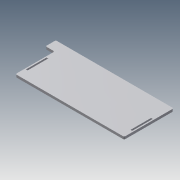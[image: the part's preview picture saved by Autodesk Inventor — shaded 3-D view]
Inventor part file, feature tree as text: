
AUTODESK INVENTOR PART (.ipt)
format: ipt  version: 2014 (Build 180170000, 170)  size: 117,248 bytes
history: native  units: mm
features: extrude x3, sketch x3, fillet x2
ambient origin geometry x8: Origin, YZ Plane, XZ Plane, XY Plane, X Axis, Y Axis, Z Axis, Center Point
bodies: Solid1 (feature_tree)
feature tree (8):
  extrude  "Extrusion1"  Depth=264.0mm
  extrude  "Extrusion2"  Depth=4.0mm
  fillet  "Fillet2"  Radius=3.0mm
  extrude  "Extrusion3"  Depth=50.0mm
  fillet  "Fillet3"  Radius=10.0mm
  sketch  "Sketch1"  dims[d0=95.0mm d1=264.0mm]
  sketch  "Sketch2"  dims[d2=6.0mm d3=0.0mm d4=4.0mm d5=3.0mm]
  sketch  "Sketch3"  dims[d6=258.0mm d7=50.0mm d8=10.0mm d9=0.0mm d11=3.0mm d12=25.0mm d13=25.0mm d15=6.0mm d16=0.0mm d17=3.0mm]
